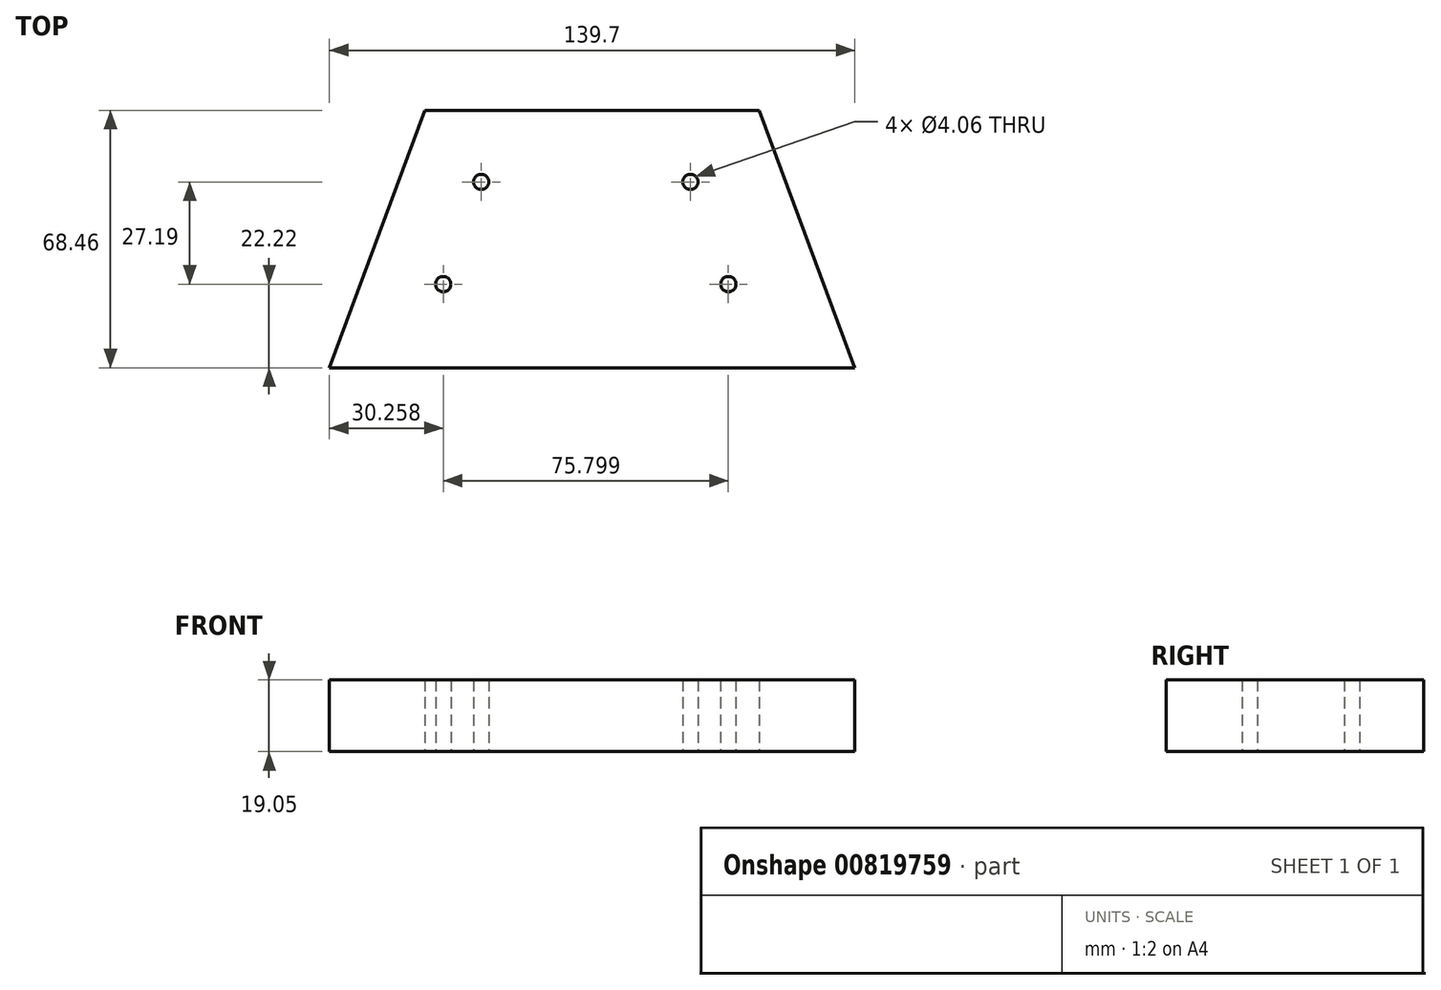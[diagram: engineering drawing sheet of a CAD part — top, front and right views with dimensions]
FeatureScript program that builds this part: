
annotation { "Feature Type Name" : "Feature", "Feature Type Description" : "" }
export const myFeature = defineFeature(function(context is Context, id is Id, definition is map)
    precondition{}
    {
        {
            var Q0;
            Q0=qCreatedBy(makeId("Top.planeOp"),FACE);
            var sketch = newSketch(context, id + "F0", { "sketchPlane" : qUnion([Q0])});
            skLineSegment(sketch, "E0", {"start": v(-82.25, -34.58) * mm, "end": v(57.45, -34.58) * mm, "construction": true});
            skLineSegment(sketch, "E1", {"start": v(57.45, -34.58) * mm, "end": v(32.05, 33.88) * mm, "construction": true});
            skLineSegment(sketch, "E2", {"start": v(32.05, 33.88) * mm, "end": v(-56.85, 33.88) * mm, "construction": true});
            skLineSegment(sketch, "E3", {"start": v(-56.85, 33.88) * mm, "end": v(-82.25, -34.58) * mm, "construction": true});
            skLineSegment(sketch, "E4", {"start": v(-56.85, 33.88) * mm, "end": v(32.05, 33.88) * mm});
            skLineSegment(sketch, "E5", {"start": v(32.05, 33.88) * mm, "end": v(57.45, -34.58) * mm});
            skLineSegment(sketch, "E6", {"start": v(57.45, -34.58) * mm, "end": v(-82.25, -34.58) * mm});
            skLineSegment(sketch, "E7", {"start": v(-82.25, -34.58) * mm, "end": v(-56.85, 33.88) * mm});
            skLineSegment(sketch, "E8", {"start": v(-74, -12.36) * mm, "end": v(49.2, -12.36) * mm, "construction": true});
            skLineSegment(sketch, "E9", {"start": v(-63.92, 14.83) * mm, "end": v(39.12, 14.83) * mm, "construction": true});
            skLineSegment(sketch, "E10", {"start": v(6.65, 33.88) * mm, "end": v(32.05, -34.58) * mm, "construction": true});
            skLineSegment(sketch, "E11", {"start": v(-34.84, 33.88) * mm, "end": v(-60.24, -34.58) * mm, "construction": true});
            skCircle(sketch, "E12", {"center": v(-41.9, 14.83) * mm, "radius": 2.03 * mm});
            skCircle(sketch, "E13", {"center": v(-52, -12.36) * mm, "radius": 2.03 * mm});
            skCircle(sketch, "E14", {"center": v(23.8, -12.36) * mm, "radius": 2.03 * mm});
            skCircle(sketch, "E15", {"center": v(13.72, 14.83) * mm, "radius": 2.03 * mm});
            skSolve(sketch);
        }
        {
            var Q0;
            Q0=makeQuery(id+"F0.imprint","IMPRINT",FACE,{"disambiguationData":[TD([[makeQuery(id+"F0.imprint","IMPRINT",EDGE,{"derivedFrom":sQuery(id+"F0.wireOp",EDGE,"E4")}),-1.0]])]});
            extrude(context, id + "F1", {"entities" : qUnion([Q0]), "depth" : 19.05 * mm, "offsetDistance" : 25.4 * mm});
        }
    });
